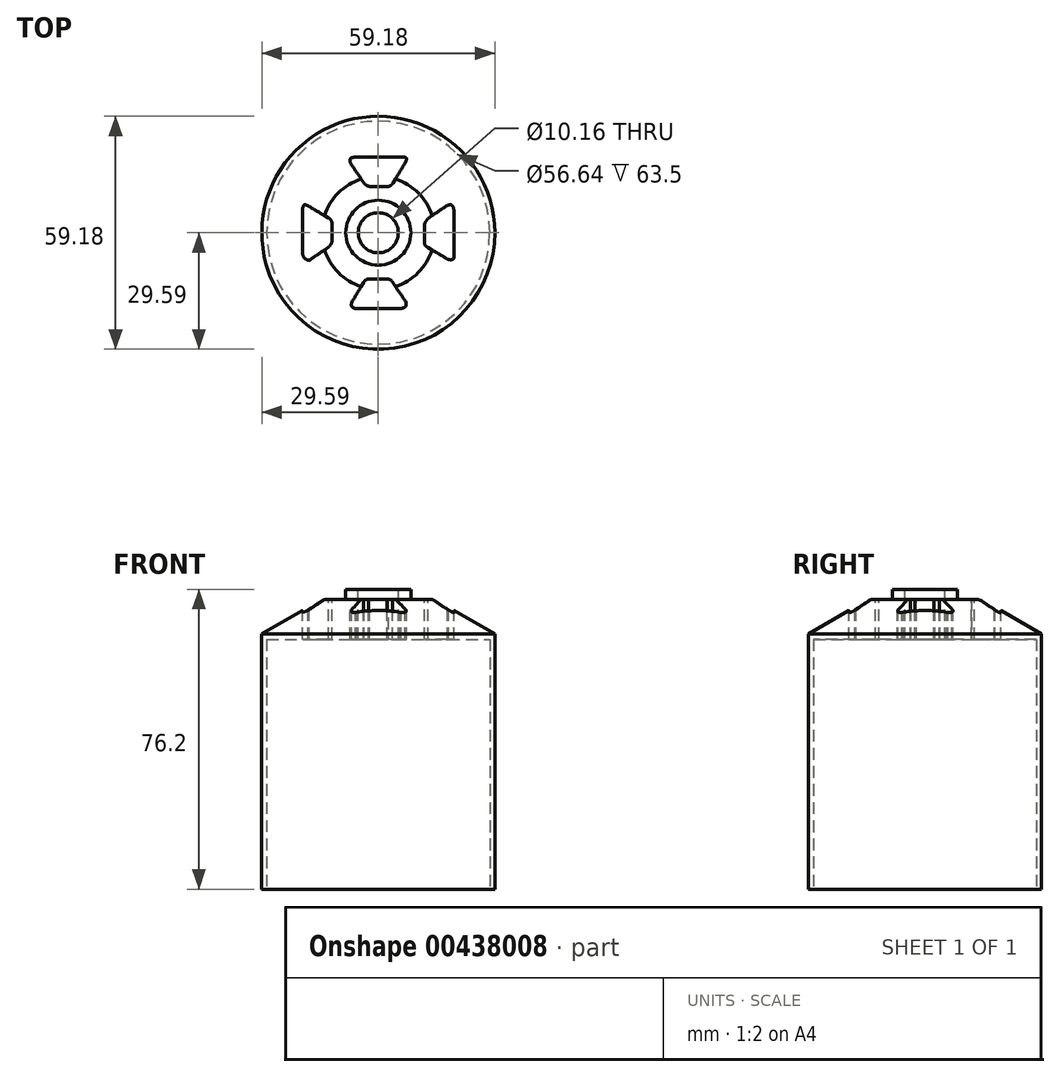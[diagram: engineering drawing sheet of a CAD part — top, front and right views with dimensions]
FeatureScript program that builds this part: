
annotation { "Feature Type Name" : "Feature", "Feature Type Description" : "" }
export const myFeature = defineFeature(function(context is Context, id is Id, definition is map)
    precondition{}
    {
        {
            var Q0;
            Q0=qCreatedBy(makeId("Top.planeOp"),FACE);
            var sketch = newSketch(context, id + "F0", { "sketchPlane" : qUnion([Q0])});
            skCircle(sketch, "E0", {"center": v(0, 0) * mm, "radius": 29.6 * mm});
            skSolve(sketch);
        }
        {
            var Q0;
            Q0=makeQuery(id+"F0.imprint","IMPRINT",FACE,{"disambiguationData":[TD([[makeQuery(id+"F0.imprint","IMPRINT",EDGE,{"derivedFrom":sQuery(id+"F0.wireOp",EDGE,"E0")}),1.0]])]});
            extrude(context, id + "F1", {"entities" : qUnion([Q0]), "depth" : 73.66 * mm});
        }
        {
            var Q0;
            Q0=makeQuery(id+"F1.opExtrude","CAP_EDGE",EDGE,{"disambiguationData":[OSD([sQuery(id+"F0.wireOp",EDGE,"E0")])],"isStart":false});
            chamfer(context, id + "F2", {"entities" : qUnion([Q0]), "chamferType" : ChamferType.OFFSET_ANGLE, "width" : 15.24 * mm, "oppositeDirection" : false, "angle" : 30 * degree, "tangentPropagation" : true});
        }
        {
            var Q0;
            Q0=makeQuery(id+"F1.opExtrude","CAP_FACE",FACE,{"disambiguationData":[OSD([sQuery(id+"F0.wireOp",EDGE,"E0")])],"isStart":false});
            var sketch = newSketch(context, id + "F3", { "sketchPlane" : qUnion([Q0])});
            skCircle(sketch, "E1", {"center": v(0, 0) * mm, "radius": 8.26 * mm});
            skSolve(sketch);
        }
        {
            var Q0;
            Q0=makeQuery(id+"F3.imprint","IMPRINT",FACE,{"disambiguationData":[TD([[makeQuery(id+"F3.imprint","IMPRINT",EDGE,{"derivedFrom":sQuery(id+"F3.wireOp",EDGE,"E1")}),1.0]])]});
            extrude(context, id + "F4", {"entities" : qUnion([Q0]), "operationType" : NewBodyOperationType.ADD, "depth" : 2.54 * mm});
        }
        {
            var Q0;
            Q0=makeQuery(id+"F4.opExtrude","CAP_FACE",FACE,{"disambiguationData":[OSD([sQuery(id+"F3.wireOp",EDGE,"E1")])],"isStart":false});
            var sketch = newSketch(context, id + "F5", { "sketchPlane" : qUnion([Q0])});
            skSolve(sketch);
        }
        {
            var Q0;
            Q0=makeQuery(id+"F5.imprint","IMPRINT",FACE,{"disambiguationData":[TD([[makeQuery(id+"F5.imprint","IMPRINT",EDGE,{"derivedFrom":makeQuery(id+"F4.opExtrude","CAP_EDGE",EDGE,{"disambiguationData":[OSD([sQuery(id+"F3.wireOp",EDGE,"E1")])],"isStart":false})}),1.0]])]});
            var sketch = newSketch(context, id + "F6", { "sketchPlane" : qUnion([Q0])});
            skCircle(sketch, "E2", {"center": v(0, 0) * mm, "radius": 5.08 * mm});
            skSolve(sketch);
        }
        {
            var Q0;
            Q0=qSketchRegion(id+"F6",true);
            extrude(context, id + "F7", {"entities" : qUnion([Q0]), "operationType" : NewBodyOperationType.REMOVE, "oppositeDirection" : true, "depth" : 25.4 * mm});
        }
        {
            var Q0;
            Q0=makeQuery(id+"F1.opExtrude","CAP_FACE",FACE,{"disambiguationData":[OSD([sQuery(id+"F0.wireOp",EDGE,"E0")])],"isStart":true});
            var sketch = newSketch(context, id + "F8", { "sketchPlane" : qUnion([Q0])});
            skCircle(sketch, "E3", {"center": v(0, 0) * mm, "radius": 28.32 * mm});
            skSolve(sketch);
        }
        {
            var Q0;
            Q0=makeQuery(id+"F8.imprint","IMPRINT",FACE,{"disambiguationData":[TD([[makeQuery(id+"F8.imprint","IMPRINT",EDGE,{"derivedFrom":sQuery(id+"F8.wireOp",EDGE,"E3")}),1.0]])]});
            extrude(context, id + "F9", {"entities" : qUnion([Q0]), "operationType" : NewBodyOperationType.REMOVE, "oppositeDirection" : true, "depth" : 63.5 * mm});
        }
        {
            var Q0;
            Q0=makeQuery(id+"F1.opExtrude","CAP_FACE",FACE,{"disambiguationData":[OSD([sQuery(id+"F0.wireOp",EDGE,"E0")])],"isStart":false});
            var sketch = newSketch(context, id + "F10", { "sketchPlane" : qUnion([Q0])});
            skLineSegment(sketch, "E4", {"start": v(-3.6, 12.59) * mm, "end": v(-7, 17.57) * mm});
            skLineSegment(sketch, "E5", {"start": v(-5.5, 19.28) * mm, "end": v(5.82, 19.28) * mm});
            skLineSegment(sketch, "E6", {"start": v(6.83, 17.81) * mm, "end": v(3.74, 12.66) * mm});
            skLineSegment(sketch, "E7", {"start": v(2.53, 11.75) * mm, "end": v(-2.25, 11.76) * mm});
            skFitSpline(sketch, "E8", {"points": [v(-7, 17.57) * mm, v(-7.23, 18.54) * mm, v(-6.9, 18.97) * mm, v(-5.5, 19.28) * mm], "startDerivative": vector(-1.12, 3.13) * mm, "endDerivative": vector(3.99, 0.53) * mm});
            skFitSpline(sketch, "E9", {"points": [v(6.83, 17.81) * mm, v(7.16, 18.66) * mm, v(6.96, 19.09) * mm, v(5.82, 19.28) * mm], "startDerivative": vector(1.3, 2.56) * mm, "endDerivative": vector(-3.43, 0.15) * mm});
            skFitSpline(sketch, "E10", {"points": [v(3.74, 12.66) * mm, v(3.2, 12.03) * mm, v(2.53, 11.75) * mm, v(2.53, 11.75) * mm], "startDerivative": vector(-0.77, -1.3) * mm, "endDerivative": vector(0.03, 0) * mm});
            skFitSpline(sketch, "E11", {"points": [v(-2.25, 11.76) * mm, v(-2.97, 12.03) * mm, v(-3.6, 12.59) * mm], "startDerivative": vector(-1.51, 0.43) * mm, "endDerivative": vector(-1.2, 1.2) * mm});
            skPoint(sketch, "E12.orphan", {"position": v(3.2, 11.74) * mm});
            skLineSegment(sketch, "E13.1.0", {"start": v(-17.81, 6.83) * mm, "end": v(-12.66, 3.74) * mm});
            skLineSegment(sketch, "E13.1.1", {"start": v(-19.28, -5.5) * mm, "end": v(-19.28, 5.82) * mm});
            skLineSegment(sketch, "E13.1.2", {"start": v(-12.59, -3.6) * mm, "end": v(-17.57, -7) * mm});
            skPoint(sketch, "E13.1.3", {"position": v(-11.74, 3.2) * mm});
            skLineSegment(sketch, "E13.1.4", {"start": v(-11.75, 2.53) * mm, "end": v(-11.76, -2.25) * mm});
            skLineSegment(sketch, "E13.2.0", {"start": v(-6.83, -17.81) * mm, "end": v(-3.74, -12.66) * mm});
            skLineSegment(sketch, "E13.2.1", {"start": v(5.5, -19.28) * mm, "end": v(-5.82, -19.28) * mm});
            skLineSegment(sketch, "E13.2.2", {"start": v(3.6, -12.59) * mm, "end": v(7, -17.57) * mm});
            skPoint(sketch, "E13.2.3", {"position": v(-3.2, -11.74) * mm});
            skLineSegment(sketch, "E13.2.4", {"start": v(-2.53, -11.75) * mm, "end": v(2.25, -11.76) * mm});
            skLineSegment(sketch, "E13.3.0", {"start": v(17.81, -6.83) * mm, "end": v(12.66, -3.74) * mm});
            skLineSegment(sketch, "E13.3.1", {"start": v(19.28, 5.5) * mm, "end": v(19.28, -5.82) * mm});
            skLineSegment(sketch, "E13.3.2", {"start": v(12.59, 3.6) * mm, "end": v(17.57, 7) * mm});
            skPoint(sketch, "E13.3.3", {"position": v(11.74, -3.2) * mm});
            skLineSegment(sketch, "E13.3.4", {"start": v(11.75, -2.53) * mm, "end": v(11.76, 2.25) * mm});
            skPoint(sketch, "E13.center", {"position": v(0, 0) * mm});
            skFitSpline(sketch, "E14", {"points": [v(11.76, 2.25) * mm, v(12.08, 2.87) * mm, v(12.59, 3.6) * mm], "startDerivative": vector(0.6, 1.3) * mm, "endDerivative": vector(1.04, 1.4) * mm});
            skFitSpline(sketch, "E15", {"points": [v(17.57, 7) * mm, v(18.65, 7) * mm, v(19.28, 5.5) * mm], "startDerivative": vector(2.68, 0.61) * mm, "endDerivative": vector(0.8, -3.48) * mm});
            skFitSpline(sketch, "E16", {"points": [v(19.28, -5.82) * mm, v(18.97, -6.74) * mm, v(17.81, -6.83) * mm], "startDerivative": vector(-0.26, -2.34) * mm, "endDerivative": vector(-2.63, 0.27) * mm});
            skFitSpline(sketch, "E17", {"points": [v(12.66, -3.74) * mm, v(11.9, -3.2) * mm, v(11.75, -2.53) * mm], "startDerivative": vector(-1.7, 0.9) * mm, "endDerivative": vector(-0.1, 1.54) * mm});
            skFitSpline(sketch, "E18", {"points": [v(3.6, -12.59) * mm, v(3.18, -12) * mm, v(2.25, -11.76) * mm], "startDerivative": vector(-0.72, 1.43) * mm, "endDerivative": vector(-1.95, 0.25) * mm});
            skFitSpline(sketch, "E19", {"points": [v(-2.53, -11.75) * mm, v(-3.19, -11.96) * mm, v(-3.74, -12.66) * mm], "startDerivative": vector(-1.48, -0.26) * mm, "endDerivative": vector(-0.95, -1.54) * mm});
            skFitSpline(sketch, "E20", {"points": [v(5.5, -19.28) * mm, v(6.87, -18.79) * mm, v(7, -17.57) * mm], "startDerivative": vector(3.22, 0.52) * mm, "endDerivative": vector(-0.26, 2.92) * mm});
            skFitSpline(sketch, "E21", {"points": [v(-5.82, -19.28) * mm, v(-6.76, -18.72) * mm, v(-6.83, -17.81) * mm], "startDerivative": vector(-2.23, 0.84) * mm, "endDerivative": vector(0.23, 2.1) * mm});
            skFitSpline(sketch, "E22", {"points": [v(-17.57, -7) * mm, v(-18.53, -6.65) * mm, v(-19.28, -5.5) * mm], "startDerivative": vector(-2.23, 0.44) * mm, "endDerivative": vector(-1.2, 2.51) * mm});
            skFitSpline(sketch, "E23", {"points": [v(-12.59, -3.6) * mm, v(-12.09, -3.03) * mm, v(-11.76, -2.25) * mm], "startDerivative": vector(1.12, 1.1) * mm, "endDerivative": vector(0.53, 1.6) * mm});
            skFitSpline(sketch, "E24", {"points": [v(-11.75, 2.53) * mm, v(-12.11, 3.34) * mm, v(-12.66, 3.74) * mm], "startDerivative": vector(-0.56, 1.7) * mm, "endDerivative": vector(-1.29, 0.7) * mm});
            skFitSpline(sketch, "E25", {"points": [v(-17.81, 6.83) * mm, v(-18.82, 7.08) * mm, v(-19.28, 5.82) * mm], "startDerivative": vector(-2.46, 1.2) * mm, "endDerivative": vector(-0.5, -3.14) * mm});
            skSolve(sketch);
        }
        {
            var Q0;
            Q0=qSketchRegion(id+"F10",true);
            var Q1;
            Q1=makeQuery(id+"F10.imprint","IMPRINT",FACE,{"disambiguationData":[TD([[makeQuery(id+"F10.imprint","IMPRINT",EDGE,{"derivedFrom":sQuery(id+"F10.wireOp",EDGE,"E13.1.1")}),-1.0]])]});
            extrude(context, id + "F11", {"entities" : qUnion([Q0, Q1]), "operationType" : NewBodyOperationType.REMOVE, "oppositeDirection" : true, "depth" : 25.4 * mm});
        }
    });
